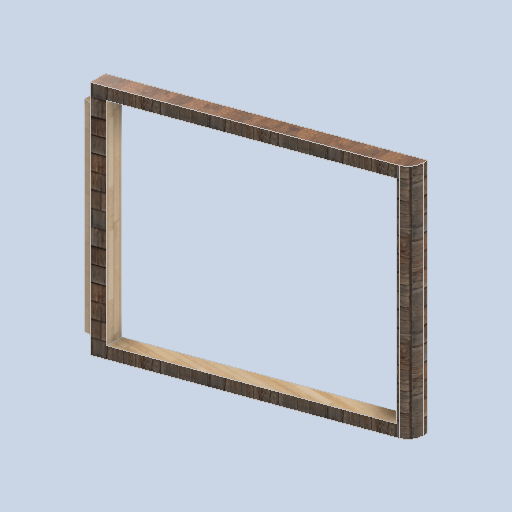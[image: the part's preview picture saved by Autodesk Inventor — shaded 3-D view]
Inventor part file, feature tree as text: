
AUTODESK INVENTOR PART (.ipt)
format: ipt  version: 2024.2 (Build 282272000, 272)  size: 397,824 bytes
history: native  units: mm
features: sketch x5, extrude x4, projected_geometry x2, plane x1, fillet x1
ambient origin geometry x8: Origin, YZ Plane, XZ Plane, XY Plane, X Axis, Y Axis, Z Axis, Center Point
bodies: Solid1 (feature_tree)
feature tree (13):
  extrude  "Extrusion1"  Depth=60.0mm TaperAngle=0.0deg
  sketch  "Sketch2"  dims[d6=2500.0mm d7=12.217305mm]
  plane  "Work Plane1"
  extrude  "Extrusion2"  Depth=12.217305mm
  extrude  "Extrusion3"  Depth=2351.0mm TaperAngle=0.0deg
  fillet  "Fillet1"  Radius=120.0mm
  extrude  "Extrusion4"  Depth=120.0mm
  sketch  "Sketch1"  dims[d3=150.0mm d4=60.0mm d5=0.0mm]
  projected_geometry  "Projected Loop1"
  sketch  "Sketch3"  dims[d8=12.217305mm d9=2351.0mm d10=0.0mm d11=120.0mm]
  sketch  "Sketch4"  dims[d12=120.0mm d13=120.0mm]
  projected_geometry  "Projected Loop2"
  sketch  "Sketch5"  dims[d14=120.0mm d15=0.0mm d16=0.0mm d17=150.0mm d18=0.0mm d19=0.0mm d20=0.0mm]
